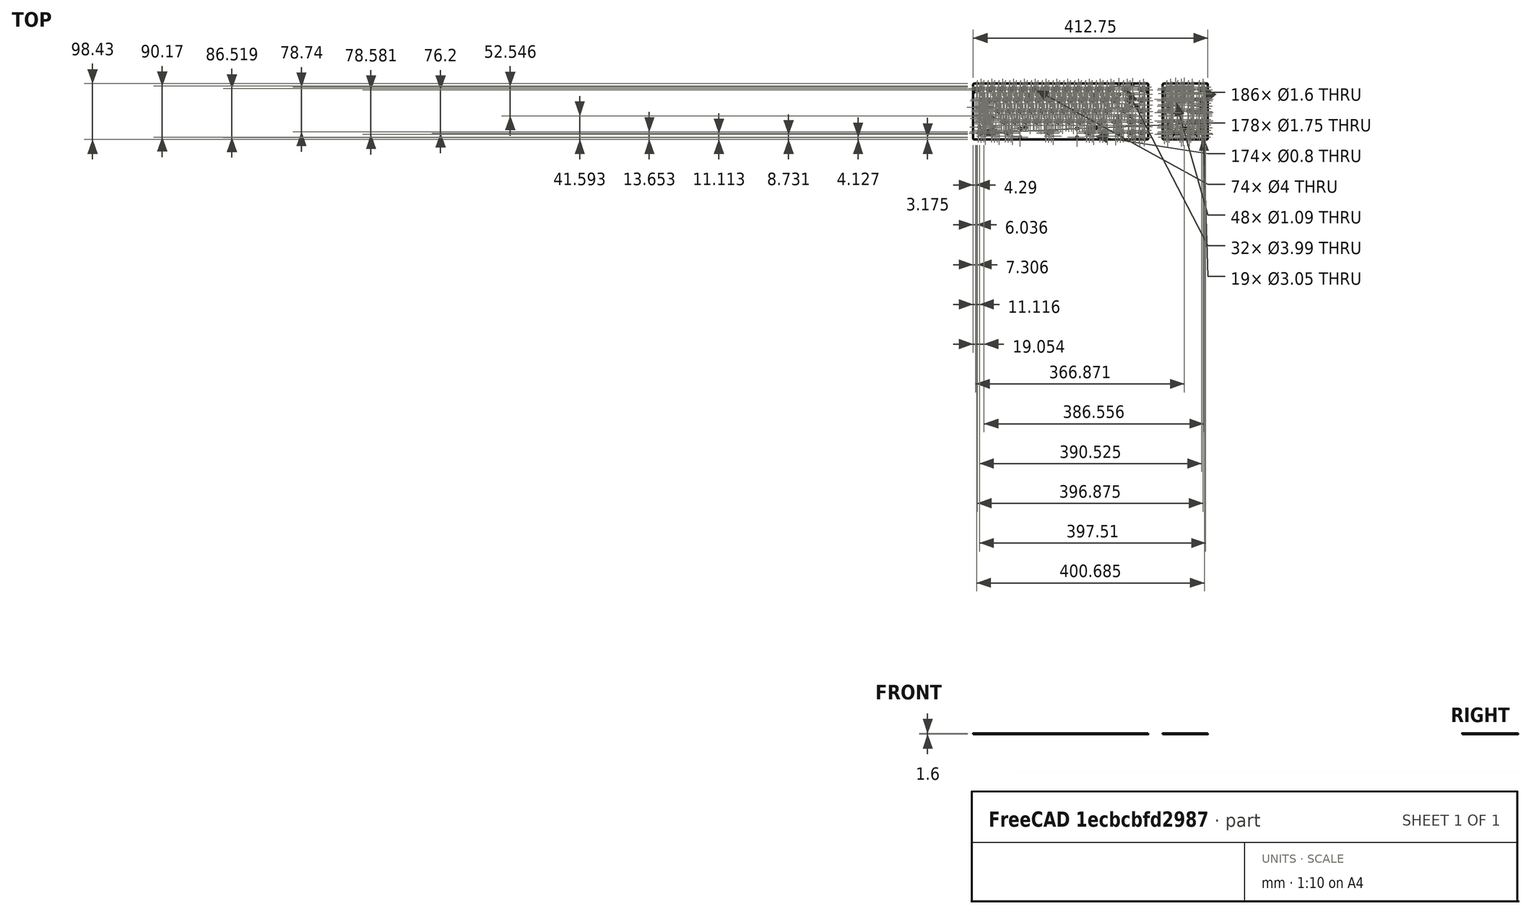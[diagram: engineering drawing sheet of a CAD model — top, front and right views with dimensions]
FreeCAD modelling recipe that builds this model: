
FCSTD DOCUMENT  (FreeCAD 0.19R23756 (Git))
Label: PCB2
License: All rights reserved
LicenseURL: http://en.wikipedia.org/wiki/All_rights_reserved
objects: Part::Feature×3, App::Part×3, PartDesign::CoordinateSystem×1, Sketcher::SketchObject×1
note: 5 computed .brp shape members not serialized (recipe doc carries the construction recipe); baked Part::Feature solids carry a one-line shape summary decoded from their .brp

FEATURE [PartDesign::CoordinateSystem] Local_CS_9e3a
  AttacherType = Attacher::AttachEngine3D
FEATURE [Part::Feature] Pcb_9e3a
  shape: bbox 412.8 x 98.43 x 1.6 mm, 790 faces, 2 solids (baked)
FEATURE [Sketcher::SketchObject] PCB_Sketch_9e3a
  FullyConstrained = false
  sketch-geometry (24):
    g0: LineSegment StartX=407.194 StartY=-67.4688 StartZ=0 EndX=407.194 EndY=-51.5938 EndZ=0
    g1: LineSegment StartX=327.819 StartY=-67.4688 StartZ=0 EndX=327.819 EndY=-51.5938 EndZ=0
    g2: LineSegment StartX=302.419 StartY=-67.4688 StartZ=0 EndX=302.419 EndY=-51.5938 EndZ=0
    g3: LineSegment StartX=-5.55625 StartY=-51.5938 StartZ=0 EndX=-5.55625 EndY=-67.4688 EndZ=0
    g4: LineSegment StartX=-5.55625 StartY=-67.4688 StartZ=0 EndX=-5.55625 EndY=-144.463 EndZ=0
    g5: LineSegment StartX=-3.96875 StartY=-146.05 StartZ=0 EndX=300.831 EndY=-146.05 EndZ=0
    g6: LineSegment StartX=-3.96875 StartY=-47.625 StartZ=0 EndX=300.831 EndY=-47.625 EndZ=0
    g7: LineSegment StartX=-5.55625 StartY=-49.2125 StartZ=0 EndX=-5.55625 EndY=-51.5938 EndZ=0
    g8: LineSegment StartX=302.419 StartY=-51.5938 StartZ=0 EndX=302.419 EndY=-49.2125 EndZ=0
    g9: LineSegment StartX=302.419 StartY=-144.462 StartZ=0 EndX=302.419 EndY=-67.4688 EndZ=0
    g10: LineSegment StartX=327.819 StartY=-49.2125 StartZ=0 EndX=327.819 EndY=-51.5938 EndZ=0
    g11: LineSegment StartX=407.194 StartY=-49.2125 StartZ=0 EndX=407.194 EndY=-51.5938 EndZ=0
    g12: LineSegment StartX=407.194 StartY=-144.462 StartZ=0 EndX=407.194 EndY=-67.4688 EndZ=0
    g13: LineSegment StartX=329.406 StartY=-146.05 StartZ=0 EndX=405.606 EndY=-146.05 EndZ=0
    g14: LineSegment StartX=327.819 StartY=-67.4688 StartZ=0 EndX=327.819 EndY=-144.463 EndZ=0
    g15: LineSegment StartX=405.606 StartY=-47.625 StartZ=0 EndX=329.406 EndY=-47.625 EndZ=0
    g16: ArcOfCircle CenterX=300.831 CenterY=-144.462 CenterZ=0 NormalX=0 NormalY=0 NormalZ=1 AngleXU=0 Radius=1.5875 StartAngle=4.71239 EndAngle=6.28319
    g17: ArcOfCircle CenterX=-3.96875 CenterY=-144.463 CenterZ=0 NormalX=0 NormalY=0 NormalZ=1 AngleXU=0 Radius=1.5875 StartAngle=3.14159 EndAngle=4.71239
    g18: ArcOfCircle CenterX=-3.96875 CenterY=-49.2125 CenterZ=0 NormalX=0 NormalY=0 NormalZ=1 AngleXU=0 Radius=1.5875 StartAngle=1.5708 EndAngle=3.14159
    g19: ArcOfCircle CenterX=300.831 CenterY=-49.2125 CenterZ=0 NormalX=0 NormalY=0 NormalZ=1 AngleXU=0 Radius=1.5875 StartAngle=0 EndAngle=1.5708
    g20: ArcOfCircle CenterX=329.406 CenterY=-144.463 CenterZ=0 NormalX=0 NormalY=0 NormalZ=1 AngleXU=0 Radius=1.5875 StartAngle=3.14159 EndAngle=4.71239
    g21: ArcOfCircle CenterX=405.606 CenterY=-144.462 CenterZ=0 NormalX=0 NormalY=0 NormalZ=1 AngleXU=0 Radius=1.5875 StartAngle=4.71239 EndAngle=6.28319
    g22: ArcOfCircle CenterX=405.606 CenterY=-49.2125 CenterZ=0 NormalX=0 NormalY=0 NormalZ=1 AngleXU=0 Radius=1.5875 StartAngle=0 EndAngle=1.5708
    g23: ArcOfCircle CenterX=329.406 CenterY=-49.2125 CenterZ=0 NormalX=0 NormalY=0 NormalZ=1 AngleXU=0 Radius=1.5875 StartAngle=1.5708 EndAngle=3.14159
  constraints (24):
    c: Coincident(g4,g17)
    c: Coincident(g3,g4)
    c: Coincident(g3,g7)
    c: Coincident(g7,g18)
    c: Coincident(g5,g17)
    c: Coincident(g6,g18)
    c: Coincident(g5,g16)
    c: Coincident(g6,g19)
    c: Coincident(g16,g9)
    c: Coincident(g2,g9)
    c: Coincident(g2,g8)
    c: Coincident(g8,g19)
    c: Coincident(g14,g20)
    c: Coincident(g1,g14)
    c: Coincident(g1,g10)
    c: Coincident(g23,g10)
    c: Coincident(g13,g20)
    c: Coincident(g15,g23)
    c: Coincident(g13,g21)
    c: Coincident(g15,g22)
    c: Coincident(g12,g21)
    c: Coincident(g0,g12)
    c: Coincident(g0,g11)
    c: Coincident(g11,g22)
FEATURE [App::Part] Step_Models_9e3a
  Origin = -> Origin002
FEATURE [Part::Feature] topTracks_9e3a
  Placement = pos=(0,0,0.01) rot=(0,0,1;0rad)
  shape: bbox 409.7 x 94.65 x 0.04 mm, 595 faces, 0 solids (baked)
FEATURE [Part::Feature] botTracks_9e3a
  Placement = pos=(0,0,-1.61) rot=(0,0,1;0rad)
  shape: bbox 409.7 x 93.09 x 0.04 mm, 648 faces, 0 solids (baked)
FEATURE [App::Part] Board_Geoms_9e3a
  Group = -> [Local_CS_9e3a,Pcb_9e3a,PCB_Sketch_9e3a,topTracks_9e3a,botTracks_9e3a]
  Origin = -> Origin
FEATURE [App::Part] Board_9e3a  label="65Numpad"
  Group = -> [Board_Geoms_9e3a,Step_Models_9e3a]
  Origin = -> Origin001
